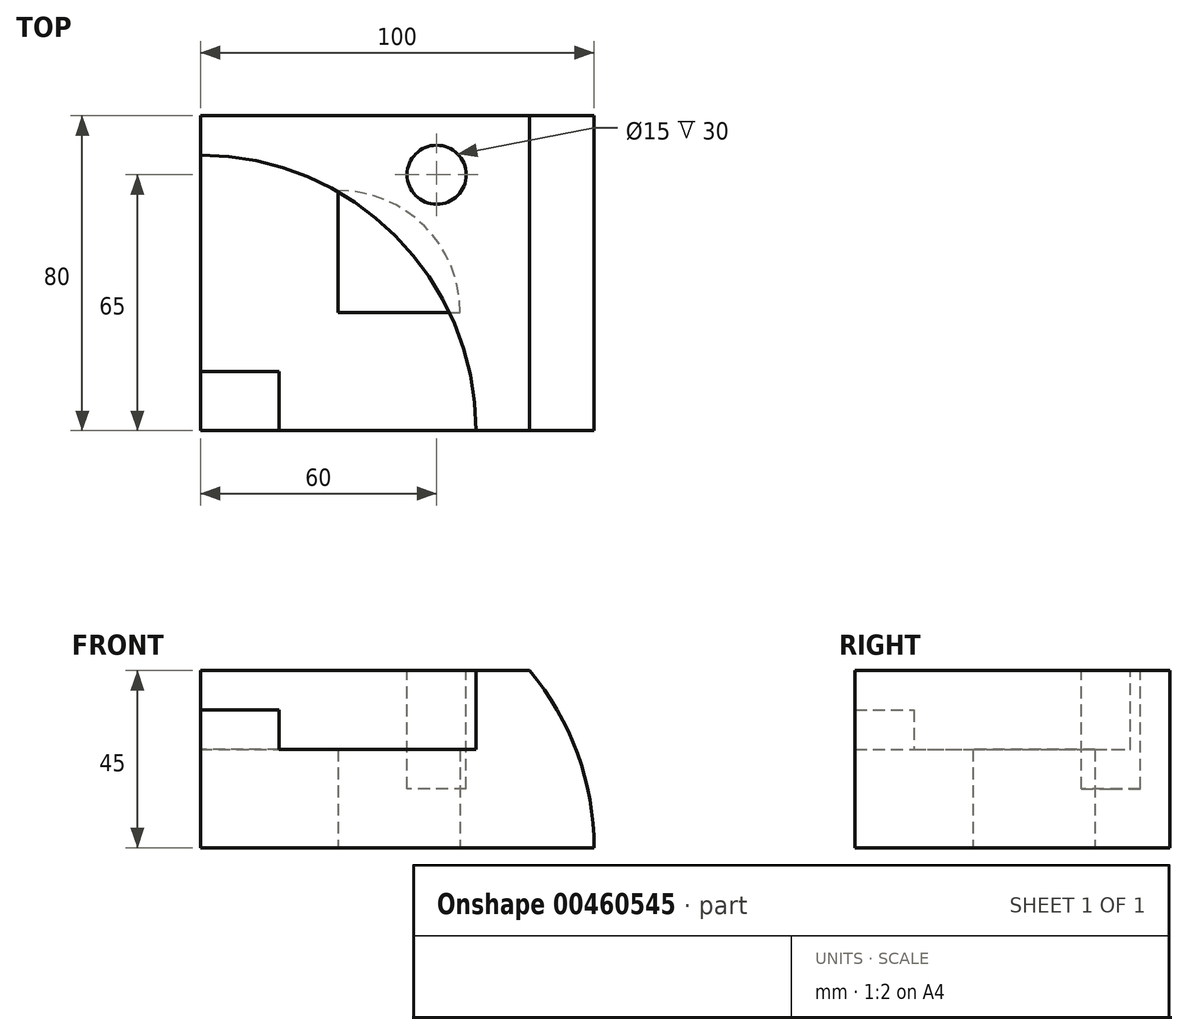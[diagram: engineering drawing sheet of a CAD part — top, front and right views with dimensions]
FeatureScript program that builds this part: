
annotation { "Feature Type Name" : "Feature", "Feature Type Description" : "" }
export const myFeature = defineFeature(function(context is Context, id is Id, definition is map)
    precondition{}
    {
        {
            var Q0;
            Q0=qCreatedBy(makeId("Front.planeOp"),FACE);
            var sketch = newSketch(context, id + "F0", { "sketchPlane" : qUnion([Q0])});
            skLineSegment(sketch, "E0.bottom", {"start": v(0, 0) * mm, "end": v(-100, 0) * mm});
            skLineSegment(sketch, "E0.top", {"start": v(0, 45) * mm, "end": v(-100, 45) * mm});
            skLineSegment(sketch, "E0.left", {"start": v(0, 0) * mm, "end": v(0, 45) * mm});
            skLineSegment(sketch, "E0.right", {"start": v(-100, 0) * mm, "end": v(-100, 45) * mm});
            skSolve(sketch);
        }
        {
            var Q0;
            Q0=makeQuery(id+"F0.imprint","IMPRINT",FACE,{"disambiguationData":[TD([[makeQuery(id+"F0.imprint","IMPRINT",EDGE,{"derivedFrom":sQuery(id+"F0.wireOp",EDGE,"E0.bottom")}),-1.0]])]});
            extrude(context, id + "F1", {"entities" : qUnion([Q0]), "depth" : 80 * mm});
        }
        {
            var Q0;
            Q0=makeQuery(id+"F1.opExtrude","SWEPT_FACE",FACE,{"disambiguationData":[OSD([sQuery(id+"F0.wireOp",EDGE,"E0.top")])]});
            var sketch = newSketch(context, id + "F2", { "sketchPlane" : qUnion([Q0])});
            skCircle(sketch, "E1", {"center": v(-40, -15) * mm, "radius": 7.5 * mm});
            skSolve(sketch);
        }
        {
            var Q0;
            Q0=makeQuery(id+"F2.imprint","IMPRINT",FACE,{"disambiguationData":[TD([[makeQuery(id+"F2.imprint","IMPRINT",EDGE,{"derivedFrom":sQuery(id+"F2.wireOp",EDGE,"E1")}),1.0]])]});
            extrude(context, id + "F3", {"entities" : qUnion([Q0]), "operationType" : NewBodyOperationType.REMOVE, "oppositeDirection" : true, "depth" : 30 * mm});
        }
        {
            var Q0;
            Q0=makeQuery(id+"F1.opExtrude","SWEPT_FACE",FACE,{"disambiguationData":[OSD([sQuery(id+"F0.wireOp",EDGE,"E0.top")])]});
            var sketch = newSketch(context, id + "F4", { "sketchPlane" : qUnion([Q0])});
            skCircle(sketch, "E2", {"center": v(-100, -80) * mm, "radius": 70 * mm});
            skSolve(sketch);
        }
        {
            var Q0;
            {var subQ0=sQuery(id+"F4.wireOp",EDGE,"E2");var subQ1=sQuery(id+"F0.wireOp",EDGE,"E0.top");var subQ4=makeQuery(id+"F1.opExtrude","CAP_EDGE",EDGE,{"disambiguationData":[OSD([subQ1])],"isStart":false});var subQ5=makeQuery(id+"F4.imprint","INTERSECT",VERTEX,{"derivedFrom":[subQ4,subQ0]});Q0=makeQuery(id+"F4.imprint","IMPRINT",FACE,{"disambiguationData":[TD([[makeQuery(id+"F4.imprint","IMPRINT",EDGE,{"disambiguationData":[TD([[subQ5,-1.0]])],"derivedFrom":subQ0}),1.0]])]});}
            extrude(context, id + "F5", {"entities" : qUnion([Q0]), "operationType" : NewBodyOperationType.REMOVE, "oppositeDirection" : true, "depth" : 20 * mm});
        }
        {
            var Q0;
            Q0=makeQuery(id+"F5.boolean.opBoolean","COPY",FACE,{"derivedFrom":makeQuery(id+"F5.opExtrude","CAP_FACE",FACE,{"disambiguationData":[OSD([sQuery(id+"F0.wireOp",EDGE,"E0.top"),sQuery(id+"F0.wireOp",EDGE,"E0.right"),sQuery(id+"F4.wireOp",EDGE,"E2")])],"isStart":false})});
            var sketch = newSketch(context, id + "F6", { "sketchPlane" : qUnion([Q0])});
            skLineSegment(sketch, "E3.bottom", {"start": v(-100, -80) * mm, "end": v(-80, -80) * mm});
            skLineSegment(sketch, "E3.top", {"start": v(-100, -65) * mm, "end": v(-80, -65) * mm});
            skLineSegment(sketch, "E3.left", {"start": v(-100, -80) * mm, "end": v(-100, -65) * mm});
            skLineSegment(sketch, "E3.right", {"start": v(-80, -80) * mm, "end": v(-80, -65) * mm});
            skSolve(sketch);
        }
        {
            var Q0;
            Q0=makeQuery(id+"F6.imprint","IMPRINT",FACE,{"disambiguationData":[TD([[makeQuery(id+"F6.imprint","IMPRINT",EDGE,{"derivedFrom":sQuery(id+"F6.wireOp",EDGE,"E3.bottom")}),-1.0]])]});
            extrude(context, id + "F7", {"entities" : qUnion([Q0]), "operationType" : NewBodyOperationType.ADD, "depth" : 10 * mm});
        }
        {
            var Q0;
            Q0=makeQuery(id+"F1.opExtrude","SWEPT_FACE",FACE,{"disambiguationData":[OSD([sQuery(id+"F0.wireOp",EDGE,"E0.bottom")])]});
            var sketch = newSketch(context, id + "F8", { "sketchPlane" : qUnion([Q0])});
            skLineSegment(sketch, "E4.left", {"start": v(-65, 50) * mm, "end": v(-65, 19) * mm});
            skLineSegment(sketch, "E5", {"start": v(-65, 50) * mm, "end": v(-34, 50) * mm});
            skCircle(sketch, "E6", {"center": v(-65, 50) * mm, "radius": 31 * mm});
            skSolve(sketch);
        }
        {
            var Q0;
            Q0=makeQuery(id+"F7.boolean.opBoolean","MERGE",FACE,{"derivedFrom":[makeQuery(id+"F1.opExtrude","CAP_FACE",FACE,{"disambiguationData":[OSD([sQuery(id+"F0.wireOp",EDGE,"E0.bottom"),sQuery(id+"F0.wireOp",EDGE,"E0.top"),sQuery(id+"F0.wireOp",EDGE,"E0.left"),sQuery(id+"F0.wireOp",EDGE,"E0.right")])],"isStart":false}),makeQuery(id+"F7.opExtrude","SWEPT_FACE",FACE,{"disambiguationData":[OSD([sQuery(id+"F6.wireOp",EDGE,"E3.bottom")])]})]});
            var sketch = newSketch(context, id + "F9", { "sketchPlane" : qUnion([Q0])});
            skCircle(sketch, "E7", {"center": v(-70, 0) * mm, "radius": 70 * mm});
            skSolve(sketch);
        }
        {
            var Q0;
            {var subQ1=makeQuery(id+"F1.opExtrude","CAP_EDGE",EDGE,{"disambiguationData":[OSD([sQuery(id+"F0.wireOp",EDGE,"E0.left")])],"isStart":false});Q0=makeQuery(id+"F9.imprint","IMPRINT",FACE,{"disambiguationData":[TD([[makeQuery(id+"F9.imprint","IMPRINT",EDGE,{"derivedFrom":subQ1}),1.0]])]});}
            extrude(context, id + "F10", {"entities" : qUnion([Q0]), "operationType" : NewBodyOperationType.REMOVE, "endBound" : BoundingType.THROUGH_ALL, "oppositeDirection" : true, "depth" : 25 * mm});
        }
        {
            var Q0;
            Q0=makeQuery(id+"F8.imprint","IMPRINT",FACE,{"disambiguationData":[TD([[makeQuery(id+"F8.imprint","IMPRINT",EDGE,{"derivedFrom":sQuery(id+"F8.wireOp",EDGE,"E4.left")}),1.0]])]});
            extrude(context, id + "F11", {"entities" : qUnion([Q0]), "operationType" : NewBodyOperationType.REMOVE, "oppositeDirection" : true, "depth" : 25 * mm});
        }
    });
